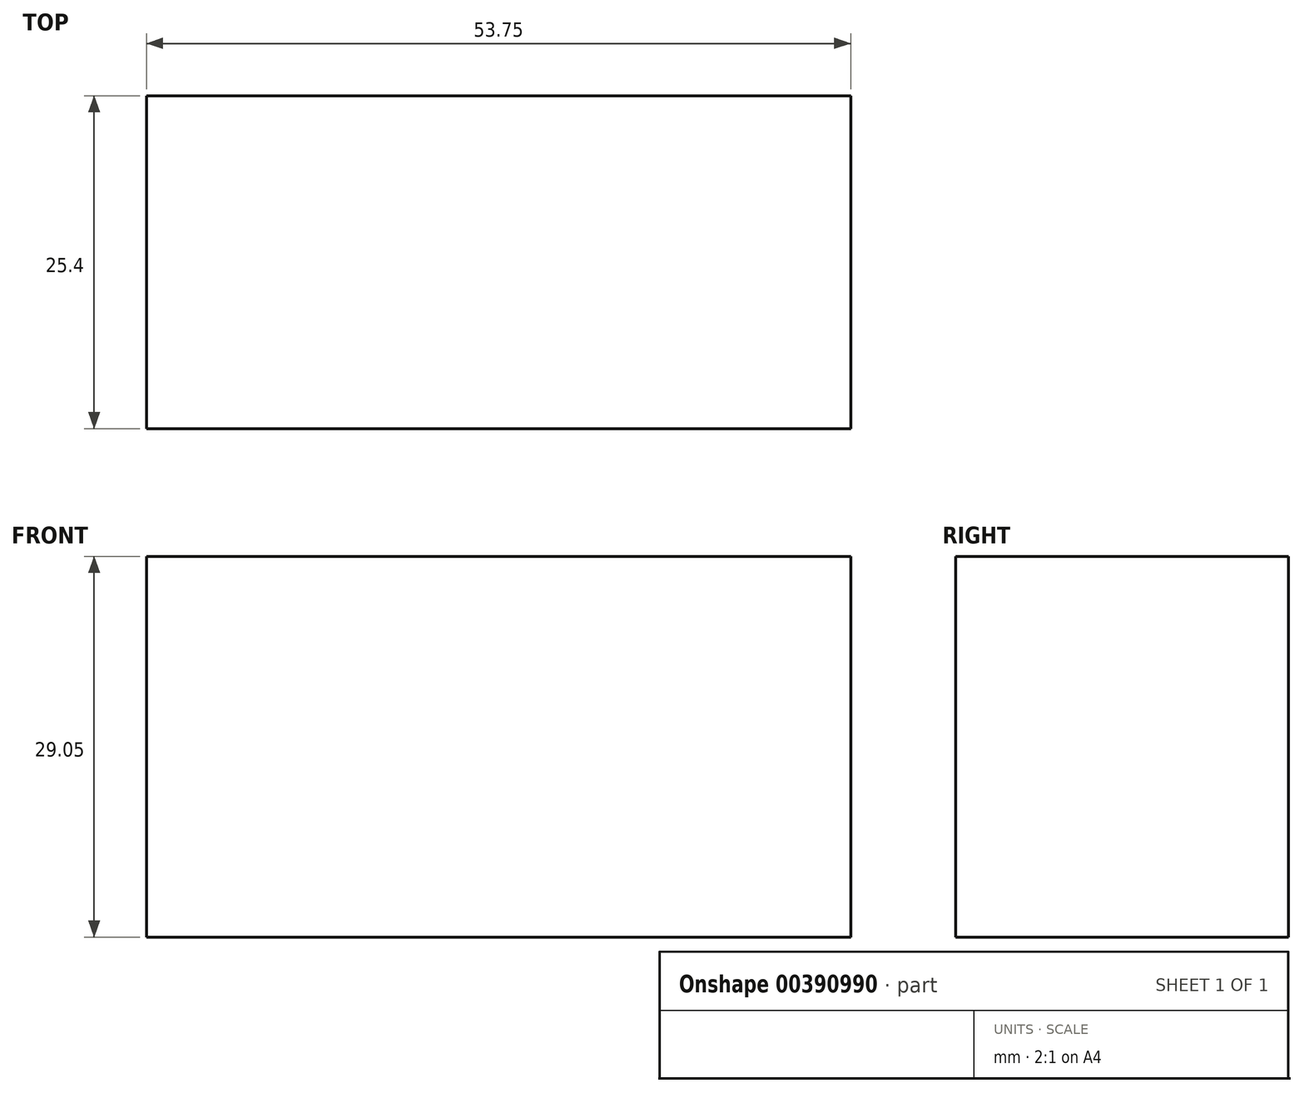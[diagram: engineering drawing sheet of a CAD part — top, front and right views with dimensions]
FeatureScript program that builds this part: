
annotation { "Feature Type Name" : "Feature", "Feature Type Description" : "" }
export const myFeature = defineFeature(function(context is Context, id is Id, definition is map)
    precondition{}
    {
        {
            var Q0;
            Q0=qCreatedBy(makeId("Front.planeOp"),FACE);
            var sketch = newSketch(context, id + "F0", { "sketchPlane" : qUnion([Q0])});
            skLineSegment(sketch, "E0.bottom", {"start": v(-99.26, 29.05) * mm, "end": v(-45.5, 29.05) * mm});
            skLineSegment(sketch, "E0.top", {"start": v(-99.26, 0) * mm, "end": v(-45.5, 0) * mm});
            skLineSegment(sketch, "E0.left", {"start": v(-99.26, 29.05) * mm, "end": v(-99.26, 0) * mm});
            skLineSegment(sketch, "E0.right", {"start": v(-45.5, 29.05) * mm, "end": v(-45.5, 0) * mm});
            skSolve(sketch);
        }
        {
            var Q0;
            Q0=makeQuery(id+"F0.imprint","IMPRINT",FACE,{"disambiguationData":[TD([[makeQuery(id+"F0.imprint","IMPRINT",EDGE,{"derivedFrom":sQuery(id+"F0.wireOp",EDGE,"E0.bottom")}),-1.0]])]});
            extrude(context, id + "F1", {"entities" : qUnion([Q0]), "depth" : 25.4 * mm});
        }
    });
